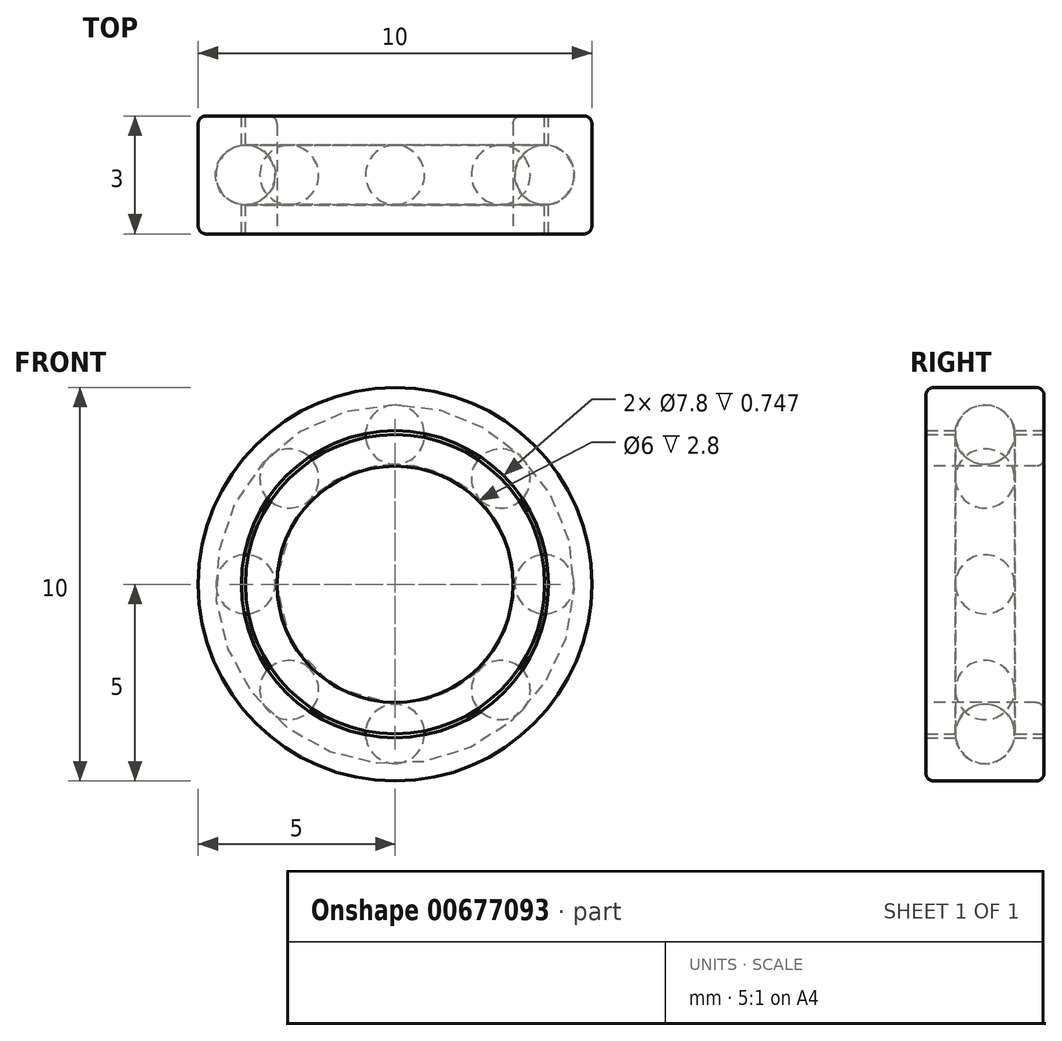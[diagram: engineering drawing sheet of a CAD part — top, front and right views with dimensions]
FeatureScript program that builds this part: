
annotation { "Feature Type Name" : "Feature", "Feature Type Description" : "" }
export const myFeature = defineFeature(function(context is Context, id is Id, definition is map)
    precondition{}
    {
        {
            var Q0;
            Q0=qCreatedBy(makeId("Right.planeOp"),FACE);
            var sketch = newSketch(context, id + "F0", { "sketchPlane" : qUnion([Q0])});
            skLineSegment(sketch, "E0.bottom", {"start": v(1.5, 0) * mm, "end": v(-1.5, 0) * mm});
            skLineSegment(sketch, "E0.top", {"start": v(1.5, 3.8) * mm, "end": v(0.76, 3.8) * mm});
            skLineSegment(sketch, "E0.left", {"start": v(1.5, 0) * mm, "end": v(1.5, 3.8) * mm});
            skLineSegment(sketch, "E0.right", {"start": v(-1.5, 0) * mm, "end": v(-1.5, 3.8) * mm});
            skLineSegment(sketch, "E1.trimOffspring", {"start": v(-0.76, 3.8) * mm, "end": v(-1.5, 3.8) * mm});
            skLineSegment(sketch, "E2.bottom", {"start": v(-1.5, 3.9) * mm, "end": v(-0.75, 3.9) * mm});
            skLineSegment(sketch, "E2.top", {"start": v(-1.5, 5) * mm, "end": v(1.5, 5) * mm});
            skLineSegment(sketch, "E2.left", {"start": v(-1.5, 3.9) * mm, "end": v(-1.5, 5) * mm});
            skLineSegment(sketch, "E2.right", {"start": v(1.5, 3.9) * mm, "end": v(1.5, 5) * mm});
            skLineSegment(sketch, "E3.trimOffspring", {"start": v(0.75, 3.9) * mm, "end": v(1.5, 3.9) * mm});
            skPoint(sketch, "E4.center.orphan", {"position": v(0, 3.9) * mm});
            skPoint(sketch, "E5.center.orphan", {"position": v(0, 3.7) * mm});
            skArc(sketch, "E6", {"start": v(-0.76, 3.8) * mm, "mid": v(0, 3.04) * mm, "end": v(0.76, 3.8) * mm});
            skArc(sketch, "E7.trimOffspring", {"start": v(0.75, 3.9) * mm, "mid": v(0, 4.56) * mm, "end": v(-0.75, 3.9) * mm});
            skPoint(sketch, "E8.orphan", {"position": v(-1, 3.8) * mm});
            skPoint(sketch, "E9.orphan", {"position": v(-1, 3.9) * mm});
            skPoint(sketch, "E10.orphan", {"position": v(1, 3.8) * mm});
            skPoint(sketch, "E11.orphan", {"position": v(1, 3.9) * mm});
            skPoint(sketch, "E12", {"position": v(1.5, 3) * mm});
            skSolve(sketch);
        }
        {
            var Q0;
            Q0=makeQuery(id+"F0.imprint","IMPRINT",FACE,{"disambiguationData":[TD([[makeQuery(id+"F0.imprint","IMPRINT",EDGE,{"derivedFrom":sQuery(id+"F0.wireOp",EDGE,"E2.bottom")}),1.0]])]});
            var Q1;
            Q1=makeQuery(id+"F0.imprint","IMPRINT",FACE,{"disambiguationData":[TD([[makeQuery(id+"F0.imprint","IMPRINT",EDGE,{"derivedFrom":sQuery(id+"F0.wireOp",EDGE,"E0.bottom")}),-1.0]])]});
            var Q2;
            Q2=sQuery(id+"F0.wireOp",EDGE,"E0.bottom");
            revolve(context, id + "F1", {"entities" : qUnion([Q0, Q1]), "axis" : qUnion([Q2]), "revolveType" : RevolveType.FULL});
        }
        {
            var Q0;
            Q0=makeQuery(id+"F1.opRevolve","SWEPT_FACE",FACE,{"disambiguationData":[OSD([sQuery(id+"F0.wireOp",EDGE,"E0.right")])]});
            var sketch = newSketch(context, id + "F2", { "sketchPlane" : qUnion([Q0])});
            skCircle(sketch, "E13", {"center": v(0, 0) * mm, "radius": 3 * mm});
            skSolve(sketch);
        }
        {
            var Q0;
            Q0 = qSketchRegion(id + "F2", true);
            extrude(context, id + "F3", {"entities" : qUnion([Q0]), "operationType" : NewBodyOperationType.REMOVE, "endBound" : BoundingType.THROUGH_ALL, "oppositeDirection" : true, "depth" : 25 * mm, "offsetDistance" : 25 * mm});
        }
        {
            var Q0;
            Q0=makeQuery(id+"F3.boolean.opBoolean","COPY",EDGE,{"derivedFrom":makeQuery(id+"F3.opExtrude","CAP_EDGE",EDGE,{"disambiguationData":[OSD([sQuery(id+"F2.wireOp",EDGE,"E13")])],"isStart":true})});
            var Q1;
            Q1=makeQuery(id+"F3.boolean.opBoolean","INTERSECT",EDGE,{"derivedFrom":[makeQuery(id+"F1.opRevolve","SWEPT_FACE",FACE,{"disambiguationData":[OSD([sQuery(id+"F0.wireOp",EDGE,"E0.left")])]}),makeQuery(id+"F3.opExtrude","SWEPT_FACE",FACE,{"disambiguationData":[OSD([sQuery(id+"F2.wireOp",EDGE,"E13")])]})]});
            var Q2;
            Q2=makeQuery(id+"F1.opRevolve","SWEPT_EDGE",EDGE,{"disambiguationData":[OSD([sQuery(id+"F0.wireOp",EDGE,"E2.top"),sQuery(id+"F0.wireOp",EDGE,"E2.right")])]});
            var Q3;
            Q3=makeQuery(id+"F1.opRevolve","SWEPT_EDGE",EDGE,{"disambiguationData":[OSD([sQuery(id+"F0.wireOp",EDGE,"E2.top"),sQuery(id+"F0.wireOp",EDGE,"E2.left")])]});
            fillet(context, id + "F4", {"entities" : qUnion([Q0, Q1, Q2, Q3]), "radius" : .2 * mm, "tangentPropagation" : true, "allowEdgeOverflow" : false});
        }
        {
            var Q0;
            Q0=qCreatedBy(makeId("Right.planeOp"),FACE);
            var sketch = newSketch(context, id + "F5", { "sketchPlane" : qUnion([Q0])});
            skArc(sketch, "E14", {"start": v(0.75, -3.8) * mm, "mid": v(0, -3.05) * mm, "end": v(-0.75, -3.8) * mm});
            skLineSegment(sketch, "E15", {"start": v(0.75, -3.8) * mm, "end": v(-0.75, -3.8) * mm});
            skSolve(sketch);
        }
        {
            var Q0;
            Q0 = qSketchRegion(id + "F5", true);
            var Q1;
            Q1=sQuery(id+"F5.wireOp",EDGE,"E15");
            revolve(context, id + "F6", {"entities" : qUnion([Q0]), "axis" : qUnion([Q1]), "revolveType" : RevolveType.FULL});
        }
        {
            var Q0;
            Q0=makeQuery(id+"F6.opRevolve","SWEPT_BODY",BODY,{"disambiguationData":[OSD([sQuery(id+"F5.wireOp",EDGE,"E14"),sQuery(id+"F5.wireOp",EDGE,"E15")])]});
            var Q1;
            Q1=qCreatedBy(makeId("Top.planeOp"),FACE);
            mirror(context, id + "F7", {"entities" : qUnion([Q0]), "mirrorPlane" : qUnion([Q1])});
        }
        {
            var Q0;
            Q0=qCreatedBy(makeId("Top.planeOp"),FACE);
            var sketch = newSketch(context, id + "F8", { "sketchPlane" : qUnion([Q0])});
            skArc(sketch, "E16", {"start": v(3.8, 0.75) * mm, "mid": v(3.05, 0) * mm, "end": v(3.8, -0.75) * mm});
            skLineSegment(sketch, "E17", {"start": v(3.8, 0.75) * mm, "end": v(3.8, -0.75) * mm});
            skSolve(sketch);
        }
        {
            var Q0;
            Q0 = qSketchRegion(id + "F8", true);
            var Q1;
            Q1=sQuery(id+"F8.wireOp",EDGE,"E17");
            revolve(context, id + "F9", {"entities" : qUnion([Q0]), "axis" : qUnion([Q1]), "revolveType" : RevolveType.FULL});
        }
        {
            var Q0;
            Q0=makeQuery(id+"F9.opRevolve","SWEPT_BODY",BODY,{"disambiguationData":[OSD([sQuery(id+"F8.wireOp",EDGE,"E16"),sQuery(id+"F8.wireOp",EDGE,"E17")])]});
            var Q1;
            Q1=qCreatedBy(makeId("Right.planeOp"),FACE);
            mirror(context, id + "F10", {"entities" : qUnion([Q0]), "mirrorPlane" : qUnion([Q1])});
        }
        {
            var Q0;
            Q0=qCreatedBy(makeId("Right.planeOp"),FACE);
            var Q1;
            Q1=qCreatedBy(makeId("Top.planeOp"),FACE);
            cPlane(context, id + "F11", {"entities" : qUnion([Q0, Q1]), "cplaneType" : CPlaneType.MID_PLANE, "offset" : 25 * mm, "width" : 150 * mm, "height" : 150 * mm});
        }
        {
            var Q0;
            Q0=qCreatedBy(makeId("Right.planeOp"),FACE);
            var Q1;
            Q1=qCreatedBy(makeId("Top.planeOp"),FACE);
            cPlane(context, id + "F12", {"entities" : qUnion([Q0, Q1]), "cplaneType" : CPlaneType.MID_PLANE, "offset" : 25 * mm, "flipAlignment" : true, "width" : 150 * mm, "height" : 150 * mm});
        }
        {
            var Q0;
            Q0=qCreatedBy(id+"F11.planeOp",FACE);
            var sketch = newSketch(context, id + "F13", { "sketchPlane" : qUnion([Q0])});
            skArc(sketch, "E18", {"start": v(0.75, -3.8) * mm, "mid": v(0, -3.05) * mm, "end": v(-0.75, -3.8) * mm});
            skLineSegment(sketch, "E19", {"start": v(-0.75, -3.8) * mm, "end": v(0.75, -3.8) * mm});
            skSolve(sketch);
        }
        {
            var Q0;
            Q0 = qSketchRegion(id + "F13", true);
            var Q1;
            Q1=sQuery(id+"F13.wireOp",EDGE,"E19");
            revolve(context, id + "F14", {"entities" : qUnion([Q0]), "axis" : qUnion([Q1]), "revolveType" : RevolveType.FULL});
        }
        {
            var Q0;
            Q0=makeQuery(id+"F14.opRevolve","SWEPT_BODY",BODY,{"disambiguationData":[OSD([sQuery(id+"F13.wireOp",EDGE,"E18"),sQuery(id+"F13.wireOp",EDGE,"E19")])]});
            var Q1;
            Q1=qCreatedBy(id+"F12.planeOp",FACE);
            mirror(context, id + "F15", {"entities" : qUnion([Q0]), "mirrorPlane" : qUnion([Q1])});
        }
        {
            var Q0;
            Q0=qCreatedBy(id+"F12.planeOp",FACE);
            var sketch = newSketch(context, id + "F16", { "sketchPlane" : qUnion([Q0])});
            skArc(sketch, "E20", {"start": v(0.75, -3.8) * mm, "mid": v(0, -3.05) * mm, "end": v(-0.75, -3.8) * mm});
            skLineSegment(sketch, "E21", {"start": v(0.75, -3.8) * mm, "end": v(-0.75, -3.8) * mm});
            skSolve(sketch);
        }
        {
            var Q0;
            Q0 = qSketchRegion(id + "F16", true);
            var Q1;
            Q1=sQuery(id+"F16.wireOp",EDGE,"E21");
            revolve(context, id + "F17", {"entities" : qUnion([Q0]), "axis" : qUnion([Q1]), "revolveType" : RevolveType.FULL});
        }
        {
            var Q0;
            Q0=makeQuery(id+"F17.opRevolve","SWEPT_BODY",BODY,{"disambiguationData":[OSD([sQuery(id+"F16.wireOp",EDGE,"E20"),sQuery(id+"F16.wireOp",EDGE,"E21")])]});
            var Q1;
            Q1=qCreatedBy(id+"F11.planeOp",FACE);
            mirror(context, id + "F18", {"entities" : qUnion([Q0]), "mirrorPlane" : qUnion([Q1])});
        }
    });
